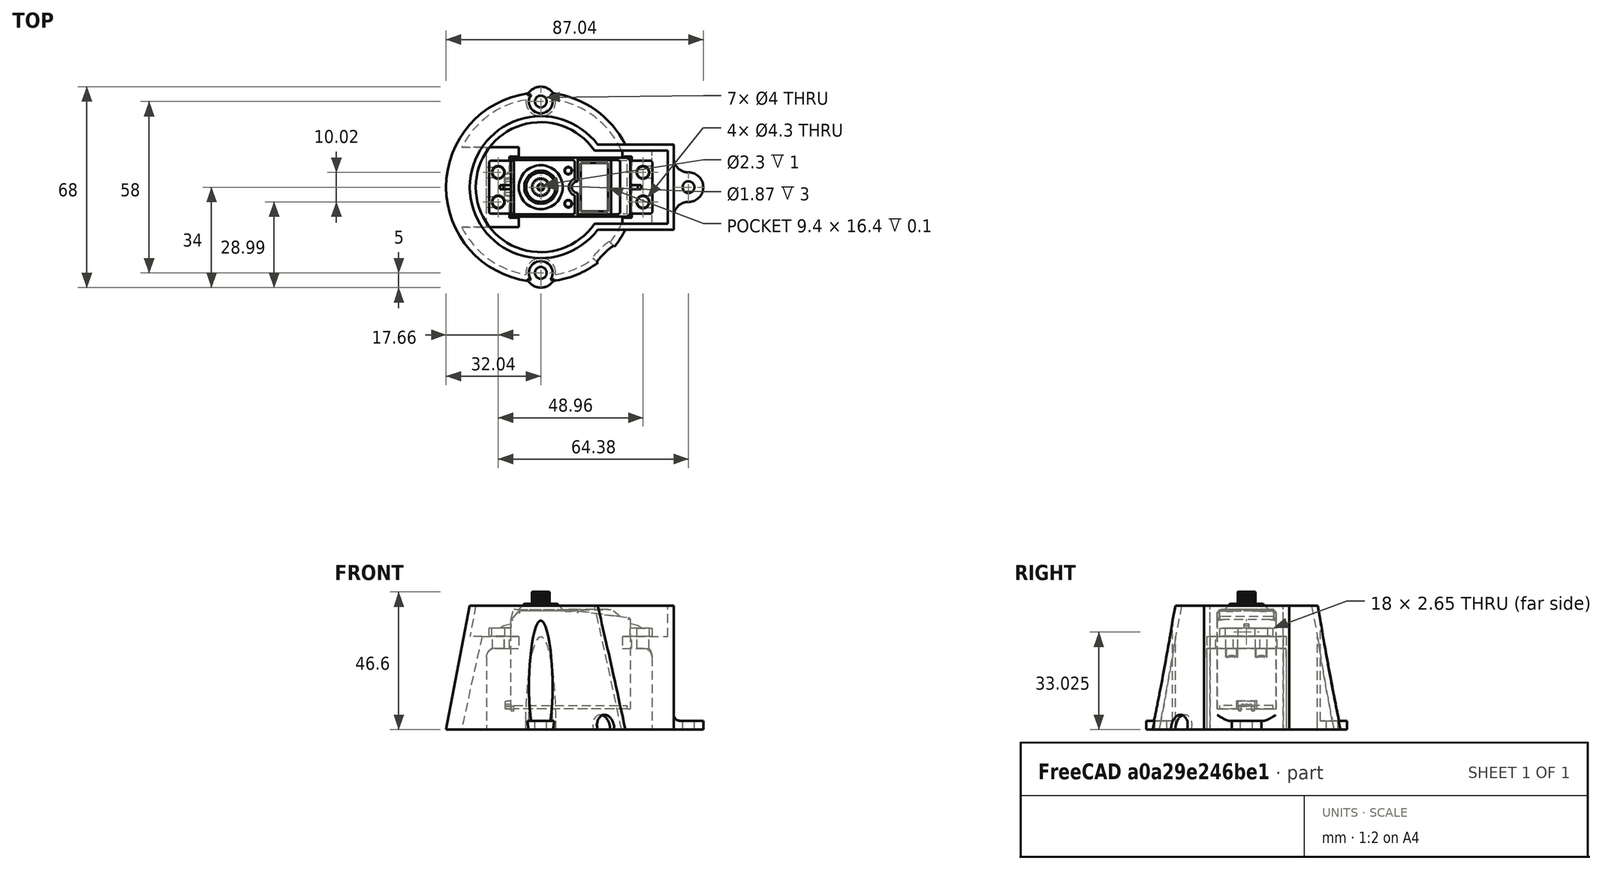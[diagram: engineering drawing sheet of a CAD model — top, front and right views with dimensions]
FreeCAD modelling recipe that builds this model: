
FCSTD DOCUMENT  (FreeCAD 0.16R6706 (Git))
Label: pieza5V4
License: CreativeCommons Attribution-ShareAlike
LicenseURL: http://creativecommons.org/licenses/by-sa/4.0/
objects: Part::Cylinder×15, Part::Cut×12, Part::MultiFuse×9, Part::Box×6, Part::Fillet×4, Part::Feature×3, Part::MultiCommon×2
note: 51 computed .brp shape members not serialized (recipe doc carries the construction recipe); baked Part::Feature solids carry a one-line shape summary decoded from their .brp

FEATURE [Part::Feature] Thickness001
  shape: bbox 77.04 x 64.07 x 42 mm, 10 faces (baked)
FEATURE [Part::Cylinder] Cylinder001  label="Cilindro001"
  Angle = 360
  Height = 3
  Placement = pos=(-3.1,-25.5,-1) rot=(0,0,1;0rad)
  Radius = 5
FEATURE [Part::Cylinder] Cylinder002  label="Cilindro002"
  Angle = 360
  Height = 3
  Placement = pos=(-3.1,32.5,-1) rot=(0,0,1;0rad)
  Radius = 5
FEATURE [Part::Cylinder] Cylinder  label="taladro1"
  Angle = 360
  Height = 45
  Placement = pos=(-3.1,-25.5,-2) rot=(0,0,1;0rad)
  Radius = 2
FEATURE [Part::Cylinder] Cylinder003  label="Taladro2"
  Angle = 360
  Height = 45
  Placement = pos=(-3.1,32.5,-2) rot=(0,0,1;0rad)
  Radius = 2
FEATURE [Part::Cylinder] Cylinder004  label="Cilindro004"
  Angle = 360
  Height = 42
  Placement = pos=(-3.1,-25.5,-1) rot=(0,0,1;0rad)
  Radius = 4
FEATURE [Part::Cylinder] Cylinder005  label="Cilindro005"
  Angle = 360
  Height = 42
  Placement = pos=(-3.1,32.5,-1) rot=(0,0,1;0rad)
  Radius = 4
FEATURE [Part::MultiFuse] Fusion001
FEATURE [Part::Cylinder] Cylinder006  label="Cilindro006"
  Angle = 360
  Height = 42
  Placement = pos=(-3.1,32.5,-1) rot=(0,0,1;0rad)
  Radius = 5
FEATURE [Part::Cylinder] Cylinder007  label="Cilindro007"
  Angle = 360
  Height = 42
  Placement = pos=(-3.1,-25.5,-1) rot=(0,0,1;0rad)
  Radius = 5
FEATURE [Part::MultiFuse] Fusion
  Shapes = -> [Cylinder006,Cylinder007]
FEATURE [Part::MultiCommon] Common
  Shapes = -> [Fusion001,Fusion]
FEATURE [Part::MultiFuse] Fusion003
  Shapes = -> [Thickness001,Common]
FEATURE [Part::MultiFuse] Fusion005
  Shapes = -> [Cylinder003,Cylinder]
FEATURE [Part::MultiFuse] Fusion006
  Shapes = -> [Cylinder002,Cylinder001]
FEATURE [Part::MultiFuse] Fusion007
  Shapes = -> [Cylinder005,Cylinder004]
FEATURE [Part::Cut] Cut
  Base = -> Fusion003
  Tool = -> Fusion007
FEATURE [Part::MultiFuse] Fusion008
  Shapes = -> [Cut,Fusion006]
FEATURE [Part::Cut] Cut001
  Base = -> Fusion008
  Tool = -> Fusion005
FEATURE [Part::Cylinder] Cylinder008  label="Cilindro008"
  Angle = 360
  Height = 3
  Placement = pos=(46.9,3.5,-1) rot=(0,0,1;0rad)
  Radius = 5
FEATURE [Part::Box] Box  label="Cubo"
  Height = 3
  Length = 5
  Placement = pos=(41.9,-1.5,-1) rot=(0,0,1;0rad)
  Width = 10
FEATURE [Part::MultiFuse] Fusion009
  Shapes = -> [Cylinder008,Box,Cut001]
FEATURE [Part::Cylinder] Cylinder009  label="Taladro003"
  Angle = 360
  Height = 45
  Placement = pos=(46.9,3.5,-3) rot=(0,0,1;0rad)
  Radius = 2
FEATURE [Part::Cut] Cut002
  Base = -> Fusion009
  Tool = -> Cylinder009
FEATURE [Part::Fillet] Fillet
  Base = -> Cut002
  Edges = 2 edges r=4.9: [Edge13,Edge20]
FEATURE [Part::Fillet] Fillet001
  Base = -> Fillet
  Edges = 1 edges r=2: [Edge15]
FEATURE [Part::Feature] Cut013004  label="Futaba-3003-body-base003"
  Placement = pos=(7,3.5,6) rot=(0,0,1;3.14159rad)
  shape: bbox 55.26 x 20 x 40.28 mm, 242 faces (baked)
FEATURE [Part::Box] Box001  label="Cubo001"
  Height = 31.5
  Length = 82
  Placement = pos=(-42,-10,-1) rot=(0,0,1;0rad)
  Width = 27
FEATURE [Part::Box] Box002  label="Cubo002"
  Height = 50
  Length = 35
  Placement = pos=(-10.5,-13,-3) rot=(0,0,1;0rad)
  Width = 37
FEATURE [Part::Cut] Cut003
  Base = -> Box001
  Tool = -> Box002
FEATURE [Part::Box] Box003  label="Cubo003"
  Height = 33
  Length = 41.4
  Placement = pos=(-13.7,-6.9,-2) rot=(0,0,1;0rad)
  Width = 20.8
FEATURE [Part::Cut] Cut013005
  Base = -> Cut003
  Tool = -> Box003
FEATURE [Part::Box] Box004  label="Cubo004"
  Height = 37
  Length = 7
  Placement = pos=(-15.4,-1,-4.5) rot=(0,0,1;0rad)
  Width = 9
FEATURE [Part::Cylinder] Cylinder013  label="Cilindro011"
  Angle = 360
  Height = 15
  Placement = pos=(31.48,8.51,19.35) rot=(0,0,1;0rad)
  Radius = 2
FEATURE [Part::Cylinder] Cylinder014  label="Cilindro012"
  Angle = 360
  Height = 15
  Placement = pos=(31.48,-1.51,19.35) rot=(0,0,1;0rad)
  Radius = 2
FEATURE [Part::Cylinder] Cylinder015  label="Cilindro013"
  Angle = 360
  Height = 15
  Placement = pos=(-17.48,-1.51,19.35) rot=(0,0,1;0rad)
  Radius = 2
FEATURE [Part::Cylinder] Cylinder016  label="Cilindro014"
  Angle = 360
  Height = 14
  Placement = pos=(-17.48,8.51,20.35) rot=(0,0,1;0rad)
  Radius = 2
FEATURE [Part::Cut] Cut013006
  Base = -> Cut013005
  Tool = -> Box004
FEATURE [Part::Cut] Cut013007
  Base = -> Cut013006
  Tool = -> Cylinder016
FEATURE [Part::Cut] Cut013008
  Base = -> Cut013007
  Tool = -> Cylinder015
FEATURE [Part::Cut] Cut013009
  Base = -> Cut013008
  Tool = -> Cylinder014
FEATURE [Part::Cut] Cut013010
  Base = -> Cut013009
  Tool = -> Cylinder013
FEATURE [Part::Box] Box007  label="Cubo007"
  Height = 56
  Length = 28.7
  Placement = pos=(-21.48,-11.34,-4.8) rot=(0.57735,0.57735,0.57735;2.0944rad)
  Width = 31.3
FEATURE [Part::Feature] Fusion012001  label="Fusion014"
  shape: bbox 73 x 60 x 42 mm, 6 faces (baked)
FEATURE [Part::Cut] Cut013011
  Base = -> Cut013010
  Tool = -> Box007
FEATURE [Part::MultiCommon] Common001
  Shapes = -> [Cut013011,Fusion012001]
FEATURE [Part::Fillet] Fillet002
  Base = -> Common001
  Edges = 1 edges r=3: [Edge46]
FEATURE [Part::Fillet] Fillet003
  Base = -> Fillet002
  Edges = 1 edges r=3: [Edge81]
FEATURE [Part::MultiFuse] Fusion012002
  Shapes = -> [Fillet001,Fillet003]
FEATURE [Part::Cylinder] Cylinder010  label="Cilindro"
  Angle = 360
  Height = 36
  Placement = pos=(0,0,0) rot=(0.361106,0.85977,-0.361106;1.72131rad)
  Radius = 4
FEATURE [Part::Cut] Cut013012
  Base = -> Fusion012002
  Tool = -> Cylinder010
